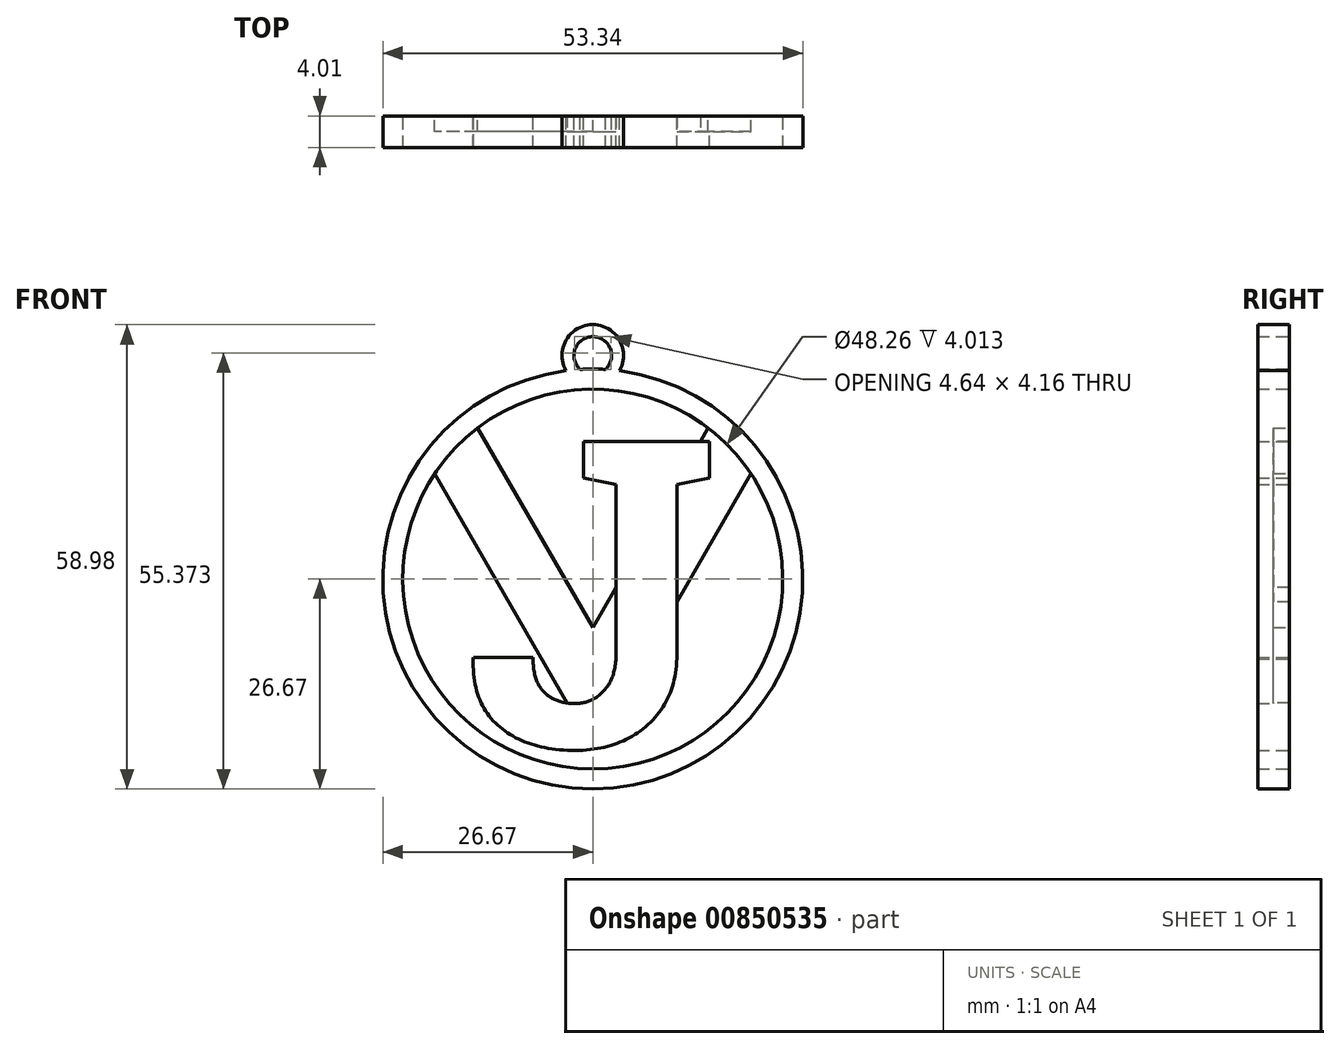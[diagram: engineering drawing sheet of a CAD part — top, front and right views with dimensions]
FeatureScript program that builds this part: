
annotation { "Feature Type Name" : "Feature", "Feature Type Description" : "" }
export const myFeature = defineFeature(function(context is Context, id is Id, definition is map)
    precondition{}
    {
        {
            var Q0;
            Q0=qCreatedBy(makeId("Front.planeOp"),FACE);
            var sketch = newSketch(context, id + "F0", { "sketchPlane" : qUnion([Q0])});
            skCircle(sketch, "E0", {"center": v(0, 0) * mm, "radius": 26.67 * mm});
            skCircle(sketch, "E1", {"center": v(0, 0) * mm, "radius": 24.13 * mm});
            skLineSegment(sketch, "E2", {"start": v(0, -24.13) * mm, "end": v(0, -6.17) * mm});
            skLineSegment(sketch, "E3", {"start": v(0, -6.17) * mm, "end": v(-14.64, 19.18) * mm});
            skLineSegment(sketch, "E4", {"start": v(0, -6.17) * mm, "end": v(14.64, 19.18) * mm});
            skLineSegment(sketch, "E5", {"start": v(0, -6.17) * mm, "end": v(0, 24.13) * mm});
            skLineSegment(sketch, "E6", {"start": v(0, -21.41) * mm, "end": v(-20.09, 13.37) * mm});
            skLineSegment(sketch, "E7", {"start": v(0, -21.41) * mm, "end": v(20.09, 13.37) * mm});
            skSolve(sketch);
        }
        {
            var Q0;
            Q0=makeQuery(id+"F0.imprint","IMPRINT",FACE,{"disambiguationData":[TD([[makeQuery(id+"F0.imprint","IMPRINT",EDGE,{"derivedFrom":sQuery(id+"F0.wireOp",EDGE,"E0")}),1.0]])]});
            var Q1;
            {var subQ0=sQuery(id+"F0.wireOp",EDGE,"E3");Q1=makeQuery(id+"F0.imprint","IMPRINT",FACE,{"disambiguationData":[TD([[makeQuery(id+"F0.imprint","IMPRINT",EDGE,{"derivedFrom":subQ0}),1.0]])]});}
            var Q2;
            {var subQ0=sQuery(id+"F0.wireOp",EDGE,"E4");Q2=makeQuery(id+"F0.imprint","IMPRINT",FACE,{"disambiguationData":[TD([[makeQuery(id+"F0.imprint","IMPRINT",EDGE,{"derivedFrom":subQ0}),-1.0]])]});}
            extrude(context, id + "F1", {"entities" : qUnion([Q0, Q1, Q2]), "depth" : 2 * mm, "offsetDistance" : 25.4 * mm});
        }
        {
            var Q0;
            Q0=makeQuery(id+"F1.opExtrude","CAP_FACE",FACE,{"disambiguationData":[OSD([sQuery(id+"F0.wireOp",EDGE,"E0"),sQuery(id+"F0.wireOp",EDGE,"E1"),sQuery(id+"F0.wireOp",EDGE,"E3"),sQuery(id+"F0.wireOp",EDGE,"E4"),sQuery(id+"F0.wireOp",EDGE,"E6"),sQuery(id+"F0.wireOp",EDGE,"E7")])],"isStart":false});
            var sketch = newSketch(context, id + "F2", { "sketchPlane" : qUnion([Q0])});
            skCircle(sketch, "E8", {"center": v(0, 0) * mm, "radius": 26.67 * mm});
            skCircle(sketch, "E9", {"center": v(0, 0) * mm, "radius": 24.13 * mm});
            skLineSegment(sketch, "E10", {"start": v(0, -24.13) * mm, "end": v(0, -6.17) * mm});
            skLineSegment(sketch, "E11", {"start": v(0, -6.17) * mm, "end": v(-14.64, 19.18) * mm});
            skLineSegment(sketch, "E12", {"start": v(0, -6.17) * mm, "end": v(14.64, 19.18) * mm});
            skLineSegment(sketch, "E13", {"start": v(0, -6.17) * mm, "end": v(0, 24.13) * mm});
            skLineSegment(sketch, "E14", {"start": v(0, -21.41) * mm, "end": v(-20.09, 13.37) * mm});
            skLineSegment(sketch, "E15", {"start": v(0, -21.41) * mm, "end": v(20.09, 13.37) * mm});
            skSolve(sketch);
        }
        {
            var Q0;
            Q0=makeQuery(id+"F2.imprint","IMPRINT",FACE,{"disambiguationData":[TD([[makeQuery(id+"F2.imprint","IMPRINT",EDGE,{"derivedFrom":sQuery(id+"F2.wireOp",EDGE,"E8")}),1.0]])]});
            extrude(context, id + "F3", {"entities" : qUnion([Q0]), "operationType" : NewBodyOperationType.ADD, "depth" : 2 * mm, "offsetDistance" : 25.4 * mm});
        }
        {
            var Q0;
            Q0=makeQuery(id+"F1.opExtrude","CAP_FACE",FACE,{"disambiguationData":[OSD([sQuery(id+"F0.wireOp",EDGE,"E0"),sQuery(id+"F0.wireOp",EDGE,"E1"),sQuery(id+"F0.wireOp",EDGE,"E3"),sQuery(id+"F0.wireOp",EDGE,"E4"),sQuery(id+"F0.wireOp",EDGE,"E6"),sQuery(id+"F0.wireOp",EDGE,"E7")])],"isStart":false});
            var sketch = newSketch(context, id + "F4", { "sketchPlane" : qUnion([Q0])});
            skText(sketch, "E16", { "text": "J", "fontName": "RobotoSlab-Bold.ttf"});
            const initialGuessF4  = {"E16": [-0.01613, -0.02121, 1, 0, 0.03918]};
            skSetInitialGuess(sketch, initialGuessF4);
            skSolve(sketch);
        }
        {
            var Q0;
            {var subQ1=sQuery(id+"F4.wireOp",EDGE,"E16.sketch_text.stroke-14");Q0=makeQuery(id+"F4.imprint","IMPRINT",FACE,{"disambiguationData":[TD([[makeQuery(id+"F4.imprint","IMPRINT",EDGE,{"derivedFrom":subQ1}),-1.0]])]});}
            var Q1;
            {var subQ10=sQuery(id+"F4.wireOp",EDGE,"E16.sketch_text.stroke-0");Q1=makeQuery(id+"F4.imprint","IMPRINT",FACE,{"disambiguationData":[TD([[makeQuery(id+"F4.imprint","IMPRINT",EDGE,{"derivedFrom":subQ10}),-1.0]])]});}
            var Q2;
            {var subQ8=sQuery(id+"F4.wireOp",EDGE,"E16.sketch_text.stroke-3");Q2=makeQuery(id+"F4.imprint","IMPRINT",FACE,{"disambiguationData":[TD([[makeQuery(id+"F4.imprint","IMPRINT",EDGE,{"derivedFrom":subQ8}),-1.0]])]});}
            extrude(context, id + "F5", {"entities" : qUnion([Q0, Q1, Q2]), "operationType" : NewBodyOperationType.ADD, "depth" : 2 * mm, "offsetDistance" : 25.4 * mm});
        }
        {
            var Q0;
            {var subQ0=sQuery(id+"F4.wireOp",EDGE,"E16.sketch_text.stroke-14");var subQ1=sQuery(id+"F0.wireOp",EDGE,"E4");var subQ2=sQuery(id+"F4.wireOp",EDGE,"E16.sketch_text.stroke-13");var subQ3=sQuery(id+"F4.wireOp",EDGE,"E16.sketch_text.stroke-17");var subQ4=sQuery(id+"F4.wireOp",EDGE,"E16.sketch_text.stroke-16");var subQ5=sQuery(id+"F4.wireOp",EDGE,"E16.sketch_text.stroke-15");Q0=makeQuery(id+"F5.boolean.opBoolean","SPLIT",FACE,{"disambiguationData":[TD([makeQuery(id+"F1.opExtrude","SWEPT_FACE",FACE,{"disambiguationData":[OSD([subQ1])]})])],"derivedFrom":makeQuery(id+"F5.opExtrude","CAP_FACE",FACE,{"disambiguationData":[OSD([sQuery(id+"F4.wireOp",EDGE,"E16.sketch_text.stroke-0"),sQuery(id+"F4.wireOp",EDGE,"E16.sketch_text.stroke-1"),sQuery(id+"F4.wireOp",EDGE,"E16.sketch_text.stroke-2"),sQuery(id+"F4.wireOp",EDGE,"E16.sketch_text.stroke-3"),sQuery(id+"F4.wireOp",EDGE,"E16.sketch_text.stroke-4"),sQuery(id+"F4.wireOp",EDGE,"E16.sketch_text.stroke-5"),sQuery(id+"F4.wireOp",EDGE,"E16.sketch_text.stroke-6"),sQuery(id+"F4.wireOp",EDGE,"E16.sketch_text.stroke-7"),sQuery(id+"F4.wireOp",EDGE,"E16.sketch_text.stroke-8"),sQuery(id+"F4.wireOp",EDGE,"E16.sketch_text.stroke-9"),sQuery(id+"F4.wireOp",EDGE,"E16.sketch_text.stroke-10"),sQuery(id+"F4.wireOp",EDGE,"E16.sketch_text.stroke-11"),sQuery(id+"F4.wireOp",EDGE,"E16.sketch_text.stroke-12"),subQ2,subQ0,subQ5,subQ4,subQ3])],"isStart":true})});}
            var Q1;
            {var subQ0=sQuery(id+"F4.wireOp",EDGE,"E16.sketch_text.stroke-8");var subQ1=sQuery(id+"F4.wireOp",EDGE,"E16.sketch_text.stroke-7");var subQ2=sQuery(id+"F4.wireOp",EDGE,"E16.sketch_text.stroke-6");var subQ4=sQuery(id+"F0.wireOp",EDGE,"E6");var subQ5=sQuery(id+"F4.wireOp",EDGE,"E16.sketch_text.stroke-4");var subQ6=sQuery(id+"F4.wireOp",EDGE,"E16.sketch_text.stroke-3");var subQ7=sQuery(id+"F4.wireOp",EDGE,"E16.sketch_text.stroke-5");var subQ8=sQuery(id+"F4.wireOp",EDGE,"E16.sketch_text.stroke-2");var subQ9=sQuery(id+"F4.wireOp",EDGE,"E16.sketch_text.stroke-9");var subQ10=sQuery(id+"F4.wireOp",EDGE,"E16.sketch_text.stroke-10");Q1=makeQuery(id+"F5.boolean.opBoolean","SPLIT",FACE,{"disambiguationData":[TD([makeQuery(id+"F1.opExtrude","SWEPT_FACE",FACE,{"disambiguationData":[OSD([subQ4])]})])],"derivedFrom":makeQuery(id+"F5.opExtrude","CAP_FACE",FACE,{"disambiguationData":[OSD([sQuery(id+"F4.wireOp",EDGE,"E16.sketch_text.stroke-0"),sQuery(id+"F4.wireOp",EDGE,"E16.sketch_text.stroke-1"),subQ8,subQ6,subQ5,subQ7,subQ2,subQ1,subQ0,subQ9,subQ10,sQuery(id+"F4.wireOp",EDGE,"E16.sketch_text.stroke-11"),sQuery(id+"F4.wireOp",EDGE,"E16.sketch_text.stroke-12"),sQuery(id+"F4.wireOp",EDGE,"E16.sketch_text.stroke-13"),sQuery(id+"F4.wireOp",EDGE,"E16.sketch_text.stroke-14"),sQuery(id+"F4.wireOp",EDGE,"E16.sketch_text.stroke-15"),sQuery(id+"F4.wireOp",EDGE,"E16.sketch_text.stroke-16"),sQuery(id+"F4.wireOp",EDGE,"E16.sketch_text.stroke-17")])],"isStart":true})});}
            extrude(context, id + "F6", {"entities" : qUnion([Q0, Q1]), "operationType" : NewBodyOperationType.ADD, "depth" : 2 * mm, "offsetDistance" : 25.4 * mm});
        }
        {
            var Q0;
            {var subQ0=sQuery(id+"F4.wireOp",EDGE,"E16.sketch_text.stroke-8");var subQ1=sQuery(id+"F4.wireOp",EDGE,"E16.sketch_text.stroke-7");var subQ2=sQuery(id+"F4.wireOp",EDGE,"E16.sketch_text.stroke-6");var subQ3=sQuery(id+"F0.wireOp",EDGE,"E7");var subQ4=sQuery(id+"F0.wireOp",EDGE,"E6");var subQ5=sQuery(id+"F0.wireOp",EDGE,"E4");var subQ6=sQuery(id+"F0.wireOp",EDGE,"E3");var subQ7=sQuery(id+"F0.wireOp",EDGE,"E1");var subQ8=sQuery(id+"F0.wireOp",EDGE,"E0");var subQ10=sQuery(id+"F4.wireOp",EDGE,"E16.sketch_text.stroke-4");var subQ11=sQuery(id+"F4.wireOp",EDGE,"E16.sketch_text.stroke-3");var subQ12=sQuery(id+"F4.wireOp",EDGE,"E16.sketch_text.stroke-5");var subQ13=sQuery(id+"F4.wireOp",EDGE,"E16.sketch_text.stroke-2");var subQ14=sQuery(id+"F4.wireOp",EDGE,"E16.sketch_text.stroke-9");var subQ15=sQuery(id+"F4.wireOp",EDGE,"E16.sketch_text.stroke-10");var subQ16=sQuery(id+"F4.wireOp",EDGE,"E16.sketch_text.stroke-17");var subQ17=sQuery(id+"F4.wireOp",EDGE,"E16.sketch_text.stroke-16");var subQ18=sQuery(id+"F4.wireOp",EDGE,"E16.sketch_text.stroke-15");var subQ19=sQuery(id+"F4.wireOp",EDGE,"E16.sketch_text.stroke-14");var subQ20=sQuery(id+"F4.wireOp",EDGE,"E16.sketch_text.stroke-13");var subQ21=sQuery(id+"F4.wireOp",EDGE,"E16.sketch_text.stroke-12");var subQ22=sQuery(id+"F4.wireOp",EDGE,"E16.sketch_text.stroke-11");var subQ23=sQuery(id+"F4.wireOp",EDGE,"E16.sketch_text.stroke-1");var subQ24=sQuery(id+"F4.wireOp",EDGE,"E16.sketch_text.stroke-0");var subQ25=makeQuery(id+"F5.opExtrude","CAP_FACE",FACE,{"disambiguationData":[OSD([subQ24,subQ23,subQ13,subQ11,subQ10,subQ12,subQ2,subQ1,subQ0,subQ14,subQ15,subQ22,subQ21,subQ20,subQ19,subQ18,subQ17,subQ16])],"isStart":true});Q0=makeQuery(id+"F6.boolean.opBoolean","MERGE",FACE,{"derivedFrom":[makeQuery(id+"F1.opExtrude","CAP_FACE",FACE,{"disambiguationData":[OSD([subQ8,subQ7,subQ6,subQ5,subQ4,subQ3])],"isStart":true}),makeQuery(id+"F6.opExtrude","CAP_FACE",FACE,{"disambiguationData":[OSD([subQ24,subQ23,subQ13,subQ11,subQ10,subQ12,subQ2,subQ1,subQ0,subQ14,subQ15,subQ22,subQ21,subQ20,subQ19,subQ18,subQ17,subQ16]),TDD([makeQuery(id+"F5.boolean.opBoolean","SPLIT",FACE,{"disambiguationData":[TD([makeQuery(id+"F1.opExtrude","SWEPT_FACE",FACE,{"disambiguationData":[OSD([subQ5])]})])],"derivedFrom":subQ25})])],"isStart":false}),makeQuery(id+"F6.opExtrude","CAP_FACE",FACE,{"disambiguationData":[OSD([subQ24,subQ23,subQ13,subQ11,subQ10,subQ12,subQ2,subQ1,subQ0,subQ14,subQ15,subQ22,subQ21,subQ20,subQ19,subQ18,subQ17,subQ16]),TDD([makeQuery(id+"F5.boolean.opBoolean","SPLIT",FACE,{"disambiguationData":[TD([makeQuery(id+"F1.opExtrude","SWEPT_FACE",FACE,{"disambiguationData":[OSD([subQ4])]})])],"derivedFrom":subQ25})])],"isStart":false})]});}
            var sketch = newSketch(context, id + "F7", { "sketchPlane" : qUnion([Q0])});
            skCircle(sketch, "E17", {"center": v(0, 28.4) * mm, "radius": 2.39 * mm});
            skPoint(sketch, "E18", {"position": v(0, 24.13) * mm});
            skCircle(sketch, "E19", {"center": v(0, 28.4) * mm, "radius": 3.91 * mm});
            skSolve(sketch);
        }
        {
            var Q0;
            {var subQ0=sQuery(id+"F7.wireOp",EDGE,"E17");var subQ1=makeQuery(id+"F1.opExtrude","CAP_EDGE",EDGE,{"disambiguationData":[OSD([sQuery(id+"F0.wireOp",EDGE,"E0")])],"isStart":true});var subQ2=makeQuery(id+"F7.imprint","INTERSECT",VERTEX,{"disambiguationData":[OD(0.0)],"derivedFrom":[subQ1,subQ0]});Q0=makeQuery(id+"F7.imprint","IMPRINT",FACE,{"disambiguationData":[TD([[makeQuery(id+"F7.imprint","IMPRINT",EDGE,{"disambiguationData":[TD([[subQ2,-1.0]])],"derivedFrom":subQ0}),-1.0]])]});}
            extrude(context, id + "F8", {"entities" : qUnion([Q0]), "operationType" : NewBodyOperationType.ADD, "oppositeDirection" : true, "depth" : 4 * mm, "offsetDistance" : 25.4 * mm});
        }
    });
